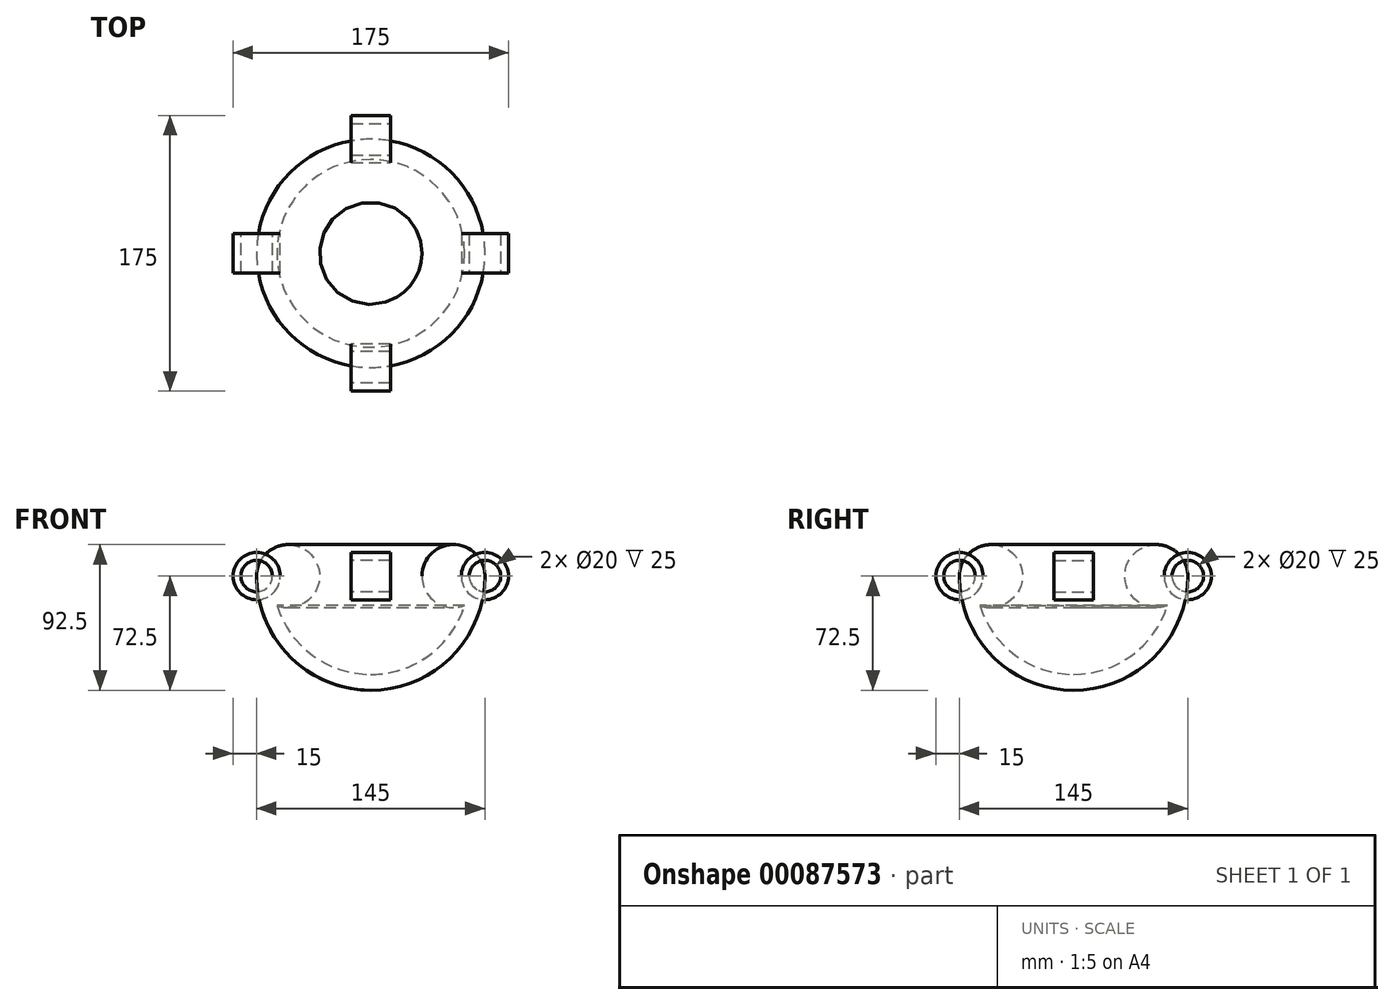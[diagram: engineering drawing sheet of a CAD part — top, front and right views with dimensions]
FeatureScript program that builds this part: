
annotation { "Feature Type Name" : "Feature", "Feature Type Description" : "" }
export const myFeature = defineFeature(function(context is Context, id is Id, definition is map)
    precondition{}
    {
        {
            var Q0;
            Q0=qCreatedBy(makeId("Front.planeOp"),FACE);
            var sketch = newSketch(context, id + "F0", { "sketchPlane" : qUnion([Q0])});
            skArc(sketch, "E0", {"start": v(72.5, 0) * mm, "mid": v(36.02, 11.34) * mm, "end": v(59.64, -18.68) * mm});
            skArc(sketch, "E1", {"start": v(0, -72.5) * mm, "mid": v(51.27, -51.27) * mm, "end": v(72.5, 0) * mm});
            skArc(sketch, "E2", {"start": v(0, -62.5) * mm, "mid": v(37, -50.37) * mm, "end": v(59.64, -18.68) * mm});
            skLineSegment(sketch, "E3", {"start": v(0, 40.7) * mm, "end": v(0, -41.35) * mm, "construction": true});
            skLineSegment(sketch, "E4", {"start": v(0, -62.5) * mm, "end": v(0, -72.5) * mm});
            skSolve(sketch);
        }
        {
            var Q0;
            Q0=qSketchRegion(id+"F0",true);
            var Q1;
            Q1=sQuery(id+"F0.wireOp",EDGE,"E3");
            revolve(context, id + "F1", {"entities" : qUnion([Q0]), "axis" : qUnion([Q1]), "revolveType" : RevolveType.FULL});
        }
        {
            var Q0;
            Q0=qCreatedBy(makeId("Front.planeOp"),FACE);
            var sketch = newSketch(context, id + "F2", { "sketchPlane" : qUnion([Q0])});
            skCircle(sketch, "E5", {"center": v(-72.5, 0) * mm, "radius": 15 * mm});
            skCircle(sketch, "E6", {"center": v(-72.5, 0) * mm, "radius": 10 * mm});
            skSolve(sketch);
        }
        {
            var Q0;
            Q0=makeQuery(id+"F2.imprint","IMPRINT",FACE,{"disambiguationData":[TD([[makeQuery(id+"F2.imprint","IMPRINT",EDGE,{"derivedFrom":sQuery(id+"F2.wireOp",EDGE,"E5")}),1.0]])]});
            extrude(context, id + "F3", {"entities" : qUnion([Q0]), "endBound" : BoundingType.SYMMETRIC, "depth" : 25 * mm});
        }
        {
            var Q0;
            Q0=makeQuery(id+"F3.opExtrude","SWEPT_BODY",BODY,{"disambiguationData":[OSD([sQuery(id+"F2.wireOp",EDGE,"E5")])]});
            var Q1;
            Q1=sQuery(id+"F0.wireOp",EDGE,"E3");
            circularPattern(context, id + "F4", {"entities" : qUnion([Q0]), "axis" : qUnion([Q1]), "angle" : 90 * degree, "instanceCount" : 4, "oppositeDirection" : true});
        }
    });
